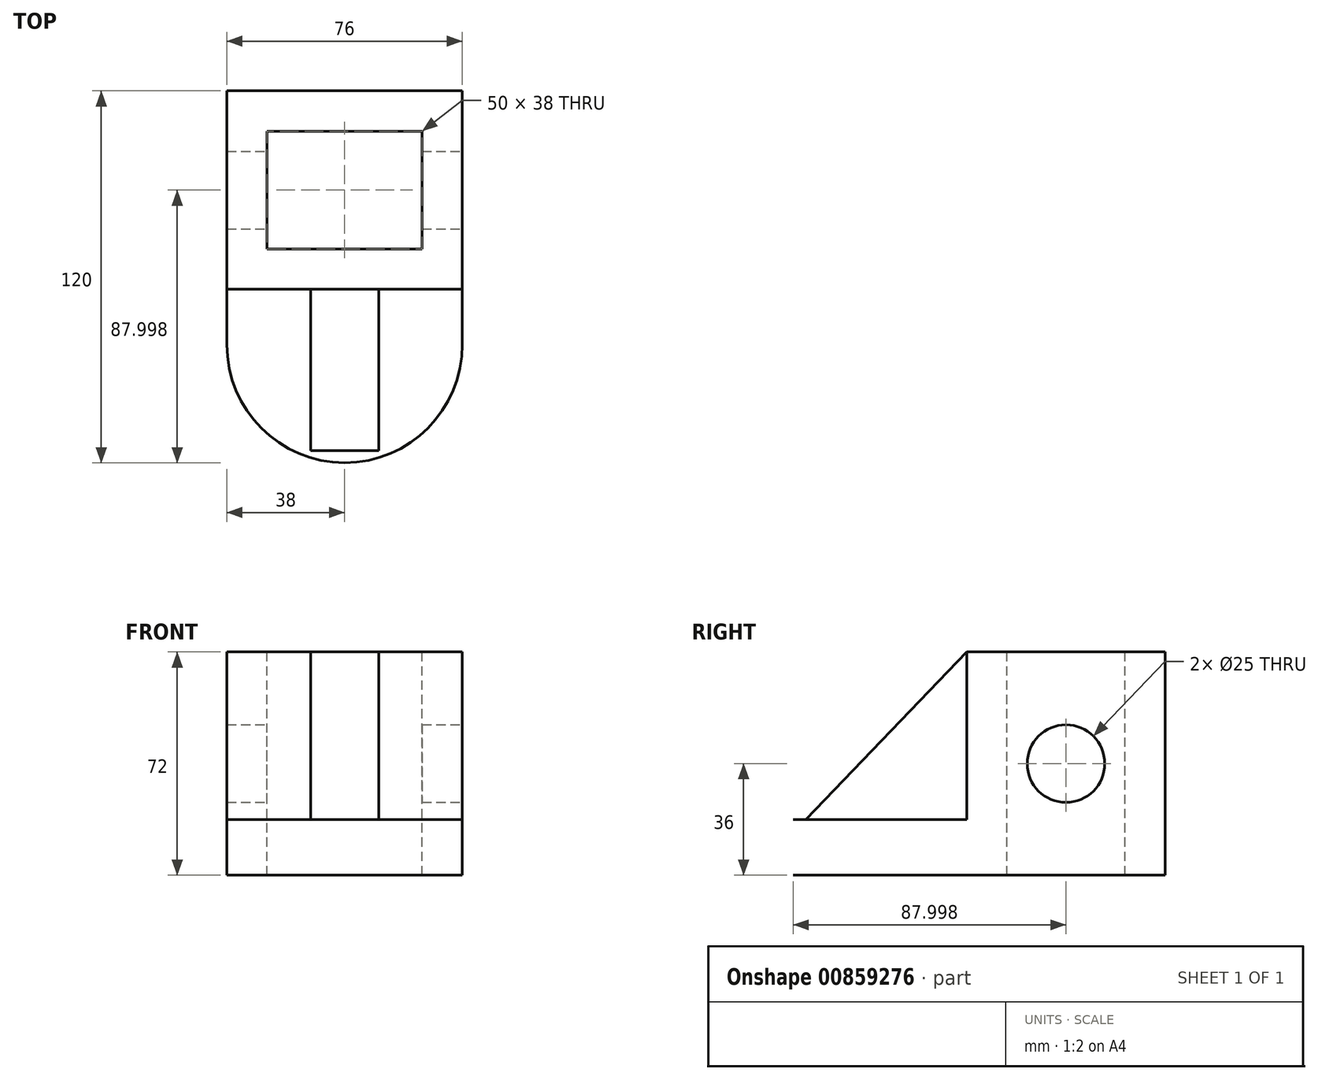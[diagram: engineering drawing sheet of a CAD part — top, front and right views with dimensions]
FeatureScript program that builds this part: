
annotation { "Feature Type Name" : "Feature", "Feature Type Description" : "" }
export const myFeature = defineFeature(function(context is Context, id is Id, definition is map)
    precondition{}
    {
        {
            var Q0;
            Q0=makeQuery(id+"FMSSpQgKYa1F4MU_0.opExtrude","SWEPT_FACE",FACE,{"disambiguationData":[OSD([sQuery(id+"FGwC6AXwwCOdoYp_0.wireOp",EDGE,"OPRynpgV-5uvH-rm8T-7i31-0rq6MHct3fj9")])]});
            var sketch = newSketch(context, id + "F0", { "sketchPlane" : qUnion([Q0])});
            skLineSegment(sketch, "E0", {"start": v(33.09, 62.37) * mm, "end": v(33.09, 17.4) * mm});
            skLineSegment(sketch, "E1", {"start": v(33.09, 17.4) * mm, "end": v(39.77, 17.4) * mm});
            skLineSegment(sketch, "E2", {"start": v(39.77, 17.4) * mm, "end": v(39.77, 62.37) * mm});
            skLineSegment(sketch, "E3", {"start": v(39.77, 62.37) * mm, "end": v(33.09, 62.37) * mm});
            skSolve(sketch);
        }
        {
            var Q0;
            Q0=qCreatedBy(makeId("Right.planeOp"),FACE);
            var sketch = newSketch(context, id + "F1", { "sketchPlane" : qUnion([Q0])});
            skLineSegment(sketch, "E4", {"start": v(-74.82, 0) * mm, "end": v(45.18, 0) * mm});
            skLineSegment(sketch, "E5", {"start": v(45.18, 0) * mm, "end": v(45.18, 72) * mm});
            skLineSegment(sketch, "E6", {"start": v(45.18, 72) * mm, "end": v(-18.82, 72) * mm});
            skLineSegment(sketch, "E7", {"start": v(-18.82, 72) * mm, "end": v(-18.82, 18) * mm});
            skLineSegment(sketch, "E8", {"start": v(-18.82, 18) * mm, "end": v(-74.82, 18) * mm});
            skLineSegment(sketch, "E9", {"start": v(-74.82, 18) * mm, "end": v(-74.82, 0) * mm});
            skSolve(sketch);
        }
        {
            var Q0;
            Q0=makeQuery(id+"F1.imprint","IMPRINT",FACE,{"disambiguationData":[TD([[makeQuery(id+"F1.imprint","IMPRINT",EDGE,{"derivedFrom":sQuery(id+"F1.wireOp",EDGE,"E4")}),1.0]])]});
            extrude(context, id + "F2", {"entities" : qUnion([Q0]), "depth" : 76 * mm, "offsetDistance" : 25 * mm});
        }
        {
            var Q0;
            Q0=makeQuery(id+"F2.opExtrude","CAP_FACE",FACE,{"disambiguationData":[OSD([sQuery(id+"F1.wireOp",EDGE,"E4"),sQuery(id+"F1.wireOp",EDGE,"E5"),sQuery(id+"F1.wireOp",EDGE,"E6"),sQuery(id+"F1.wireOp",EDGE,"E7"),sQuery(id+"F1.wireOp",EDGE,"E8"),sQuery(id+"F1.wireOp",EDGE,"E9")])],"isStart":false});
            var sketch = newSketch(context, id + "F3", { "sketchPlane" : qUnion([Q0])});
            skLineSegment(sketch, "E10", {"start": v(45.18, 0) * mm, "end": v(45.18, 36) * mm});
            skLineSegment(sketch, "E11", {"start": v(45.18, 36) * mm, "end": v(13.18, 36) * mm});
            skCircle(sketch, "E12", {"center": v(13.18, 36) * mm, "radius": 12.5 * mm});
            skSolve(sketch);
        }
        {
            var Q0;
            Q0=makeQuery(id+"F3.imprint","IMPRINT",FACE,{"disambiguationData":[TD([[makeQuery(id+"F3.imprint","IMPRINT",EDGE,{"derivedFrom":sQuery(id+"F3.wireOp",EDGE,"E12")}),1.0]])]});
            extrude(context, id + "F4", {"entities" : qUnion([Q0]), "operationType" : NewBodyOperationType.REMOVE, "oppositeDirection" : true, "depth" : 127.1 * mm, "offsetDistance" : 25 * mm});
        }
        {
            var Q0;
            Q0=makeQuery(id+"F2.opExtrude","SWEPT_FACE",FACE,{"disambiguationData":[OSD([sQuery(id+"F1.wireOp",EDGE,"E6")])]});
            var sketch = newSketch(context, id + "F5", { "sketchPlane" : qUnion([Q0])});
            skLineSegment(sketch, "E13", {"start": v(0, 13.18) * mm, "end": v(13, 13.18) * mm});
            skLineSegment(sketch, "E14", {"start": v(28.52, -18.82) * mm, "end": v(28.52, -5.82) * mm});
            skLineSegment(sketch, "E15", {"start": v(76, 16.26) * mm, "end": v(63, 16.26) * mm});
            skLineSegment(sketch, "E16", {"start": v(35.43, 45.18) * mm, "end": v(35.43, 32.18) * mm});
            skLineSegment(sketch, "E17", {"start": v(13, 13.18) * mm, "end": v(13, -18.82) * mm});
            skLineSegment(sketch, "E18", {"start": v(63, 16.26) * mm, "end": v(63, 45.18) * mm});
            skLineSegment(sketch, "E19", {"start": v(35.43, 32.18) * mm, "end": v(0, 32.18) * mm});
            skLineSegment(sketch, "E20", {"start": v(13, 13.18) * mm, "end": v(13, 32.18) * mm});
            skLineSegment(sketch, "E21", {"start": v(13, 32.18) * mm, "end": v(63, 32.18) * mm});
            skLineSegment(sketch, "E22", {"start": v(28.52, -5.82) * mm, "end": v(13, -5.82) * mm});
            skLineSegment(sketch, "E23", {"start": v(28.52, -5.82) * mm, "end": v(67.48, -5.82) * mm});
            skLineSegment(sketch, "E24", {"start": v(63, 16.26) * mm, "end": v(63, -5.82) * mm});
            skSolve(sketch);
        }
        {
            var Q0;
            {var subQ2=sQuery(id+"F5.wireOp",EDGE,"E20");Q0=makeQuery(id+"F5.imprint","IMPRINT",FACE,{"disambiguationData":[TD([[makeQuery(id+"F5.imprint","IMPRINT",EDGE,{"derivedFrom":subQ2}),-1.0]])]});}
            extrude(context, id + "F6", {"entities" : qUnion([Q0]), "operationType" : NewBodyOperationType.REMOVE, "oppositeDirection" : true, "depth" : 53.4 * mm, "offsetDistance" : 25 * mm});
        }
        {
            var Q0;
            Q0=makeQuery(id+"F2.opExtrude","CAP_EDGE",EDGE,{"disambiguationData":[OSD([sQuery(id+"F1.wireOp",EDGE,"E9")])],"isStart":true});
            var Q1;
            Q1=makeQuery(id+"F2.opExtrude","CAP_EDGE",EDGE,{"disambiguationData":[OSD([sQuery(id+"F1.wireOp",EDGE,"E9")])],"isStart":false});
            fillet(context, id + "F7", {"entities" : qUnion([Q0, Q1]), "radius" : 38.14 * mm, "tangentPropagation" : true, "allowEdgeOverflow" : false});
        }
        {
            var Q0;
            Q0=makeQuery(id+"F2.opExtrude","SWEPT_FACE",FACE,{"disambiguationData":[OSD([sQuery(id+"F1.wireOp",EDGE,"E7")])]});
            var sketch = newSketch(context, id + "F8", { "sketchPlane" : qUnion([Q0])});
            skLineSegment(sketch, "E25", {"start": v(0, 72) * mm, "end": v(38, 72) * mm});
            skLineSegment(sketch, "E26", {"start": v(38, 72) * mm, "end": v(38, 18) * mm});
            skLineSegment(sketch, "E27", {"start": v(38, 18) * mm, "end": v(27, 18) * mm});
            skLineSegment(sketch, "E28", {"start": v(38, 18) * mm, "end": v(49, 18) * mm});
            skLineSegment(sketch, "E29", {"start": v(49, 18) * mm, "end": v(49, 72) * mm});
            skLineSegment(sketch, "E30", {"start": v(49, 72) * mm, "end": v(38, 72) * mm});
            skLineSegment(sketch, "E31", {"start": v(27, 18) * mm, "end": v(27, 72) * mm});
            skLineSegment(sketch, "E32", {"start": v(27, 72) * mm, "end": v(38, 72) * mm});
            skSolve(sketch);
        }
        {
            var Q0;
            Q0=makeQuery(id+"F8.imprint","IMPRINT",FACE,{"disambiguationData":[TD([[makeQuery(id+"F8.imprint","IMPRINT",EDGE,{"derivedFrom":sQuery(id+"F8.wireOp",EDGE,"E26")}),-1.0]])]});
            extrude(context, id + "F9", {"entities" : qUnion([Q0]), "operationType" : NewBodyOperationType.ADD, "depth" : 52 * mm, "offsetDistance" : 25 * mm});
        }
        {
            var Q0;
            {var subQ2=sQuery(id+"F1.wireOp",EDGE,"E7");Q0=makeQuery(id+"F9.boolean.opBoolean","SPLIT",FACE,{"disambiguationData":[TD([makeQuery(id+"F9.opExtrude","SWEPT_FACE",FACE,{"disambiguationData":[OSD([sQuery(id+"F8.wireOp",EDGE,"E26")])]})])],"derivedFrom":makeQuery(id+"F2.opExtrude","SWEPT_FACE",FACE,{"disambiguationData":[OSD([subQ2])]})});}
            var sketch = newSketch(context, id + "F10", { "sketchPlane" : qUnion([Q0])});
            skLineSegment(sketch, "E33", {"start": v(38, 72) * mm, "end": v(49, 72) * mm});
            skLineSegment(sketch, "E34", {"start": v(49, 72) * mm, "end": v(49, 18) * mm});
            skLineSegment(sketch, "E35", {"start": v(49, 18) * mm, "end": v(38, 18) * mm});
            skLineSegment(sketch, "E36", {"start": v(38, 18) * mm, "end": v(38, 72) * mm});
            skSolve(sketch);
        }
        {
            var Q0;
            Q0=makeQuery(id+"F10.imprint","IMPRINT",FACE,{"disambiguationData":[TD([[makeQuery(id+"F10.imprint","IMPRINT",EDGE,{"derivedFrom":sQuery(id+"F10.wireOp",EDGE,"E33")}),1.0]])]});
            extrude(context, id + "F11", {"entities" : qUnion([Q0]), "operationType" : NewBodyOperationType.ADD, "depth" : 52 * mm, "offsetDistance" : 25 * mm});
        }
        {
            var Q0;
            Q0=makeQuery(id+"F11.opExtrude","SWEPT_FACE",FACE,{"disambiguationData":[OSD([sQuery(id+"F10.wireOp",EDGE,"E34")])]});
            var sketch = newSketch(context, id + "F12", { "sketchPlane" : qUnion([Q0])});
            skLineSegment(sketch, "E37", {"start": v(-70.82, 18) * mm, "end": v(-18.82, 72) * mm});
            skLineSegment(sketch, "E38", {"start": v(-18.82, 72) * mm, "end": v(-70.82, 72) * mm});
            skLineSegment(sketch, "E39", {"start": v(-70.82, 72) * mm, "end": v(-70.82, 18) * mm});
            skSolve(sketch);
        }
        {
            var Q0;
            Q0=makeQuery(id+"F12.imprint","IMPRINT",FACE,{"disambiguationData":[TD([[makeQuery(id+"F12.imprint","IMPRINT",EDGE,{"derivedFrom":sQuery(id+"F12.wireOp",EDGE,"E37")}),1.0]])]});
            extrude(context, id + "F13", {"entities" : qUnion([Q0]), "operationType" : NewBodyOperationType.REMOVE, "oppositeDirection" : true, "depth" : 67.9 * mm, "offsetDistance" : 25 * mm});
        }
        {
            var Q0;
            Q0=makeQuery(id+"F6.boolean.opBoolean","COPY",FACE,{"derivedFrom":makeQuery(id+"F6.opExtrude","CAP_FACE",FACE,{"disambiguationData":[OSD([sQuery(id+"F5.wireOp",EDGE,"E17"),sQuery(id+"F5.wireOp",EDGE,"E18"),sQuery(id+"F5.wireOp",EDGE,"E20"),sQuery(id+"F5.wireOp",EDGE,"E21"),sQuery(id+"F5.wireOp",EDGE,"E22"),sQuery(id+"F5.wireOp",EDGE,"E23"),sQuery(id+"F5.wireOp",EDGE,"E24")])],"isStart":false})});
            var sketch = newSketch(context, id + "F14", { "sketchPlane" : qUnion([Q0])});
            skLineSegment(sketch, "E40", {"start": v(13, -5.82) * mm, "end": v(13, 32.18) * mm});
            skLineSegment(sketch, "E41", {"start": v(13, 32.18) * mm, "end": v(63, 32.18) * mm});
            skLineSegment(sketch, "E42", {"start": v(63, 32.18) * mm, "end": v(63, -5.82) * mm});
            skLineSegment(sketch, "E43", {"start": v(63, -5.82) * mm, "end": v(13, -5.82) * mm});
            skSolve(sketch);
        }
        {
            var Q0;
            Q0=makeQuery(id+"F14.imprint","IMPRINT",FACE,{"disambiguationData":[TD([[makeQuery(id+"F14.imprint","IMPRINT",EDGE,{"derivedFrom":sQuery(id+"F14.wireOp",EDGE,"E40")}),-1.0]])]});
            extrude(context, id + "F15", {"entities" : qUnion([Q0]), "operationType" : NewBodyOperationType.REMOVE, "oppositeDirection" : true, "depth" : 79.6 * mm, "offsetDistance" : 25 * mm});
        }
    });
